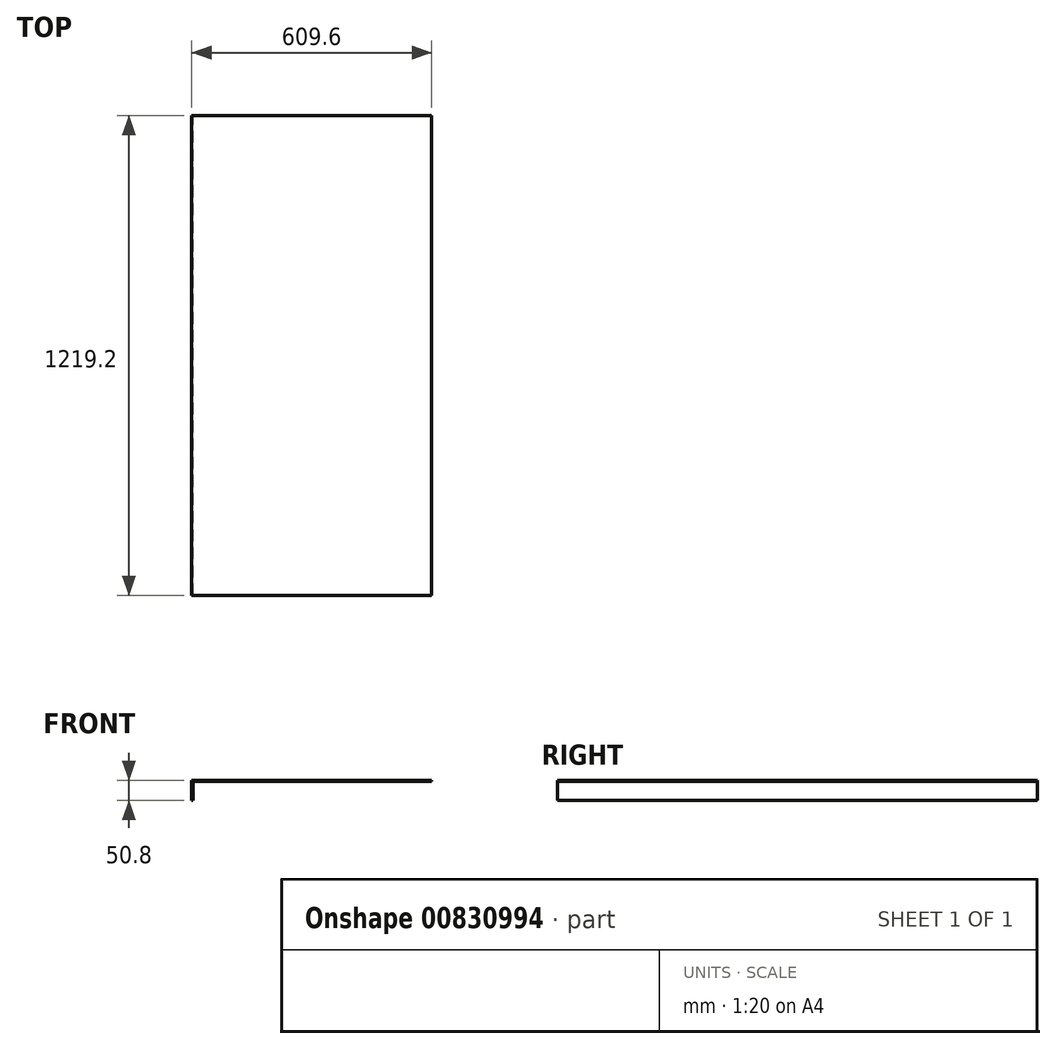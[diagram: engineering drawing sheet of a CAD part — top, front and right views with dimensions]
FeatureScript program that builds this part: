
annotation { "Feature Type Name" : "Feature", "Feature Type Description" : "" }
export const myFeature = defineFeature(function(context is Context, id is Id, definition is map)
    precondition{}
    {
        {
            var Q0;
            Q0=qCreatedBy(makeId("Front.planeOp"),FACE);
            var sketch = newSketch(context, id + "F0", { "sketchPlane" : qUnion([Q0])});
            skLineSegment(sketch, "E0", {"start": v(0, 0) * mm, "end": v(0, 50.8) * mm});
            skLineSegment(sketch, "E1", {"start": v(0, 50.8) * mm, "end": v(609.6, 50.8) * mm});
            skLineSegment(sketch, "E2", {"start": v(609.6, 50.8) * mm, "end": v(609.6, 47.63) * mm});
            skLineSegment(sketch, "E3", {"start": v(609.6, 47.63) * mm, "end": v(3.17, 47.62) * mm});
            skLineSegment(sketch, "E4", {"start": v(3.17, 47.62) * mm, "end": v(3.17, 0) * mm});
            skLineSegment(sketch, "E5", {"start": v(3.17, 0) * mm, "end": v(0, 0) * mm});
            skSolve(sketch);
        }
        {
            var Q0;
            Q0=makeQuery(id+"F0.imprint","IMPRINT",FACE,{"disambiguationData":[TD([[makeQuery(id+"F0.imprint","IMPRINT",EDGE,{"derivedFrom":sQuery(id+"F0.wireOp",EDGE,"E0")}),-1.0]])]});
            extrude(context, id + "F1", {"entities" : qUnion([Q0]), "depth" : 1219.2 * mm, "offsetDistance" : 25.4 * mm});
        }
    });
